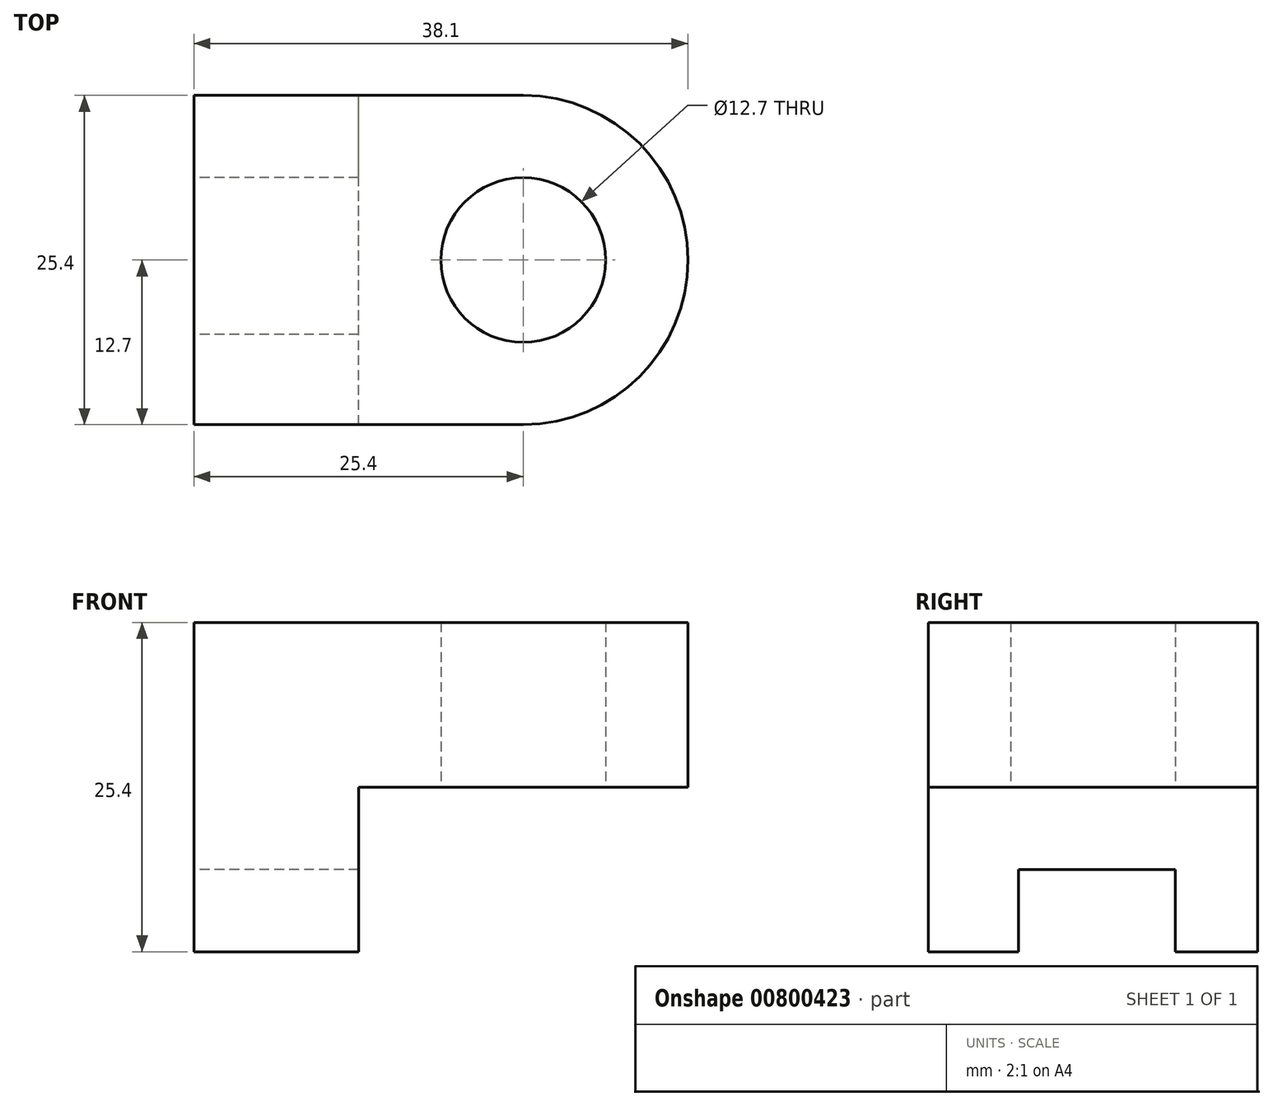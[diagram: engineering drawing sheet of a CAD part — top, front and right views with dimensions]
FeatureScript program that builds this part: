
annotation { "Feature Type Name" : "Feature", "Feature Type Description" : "" }
export const myFeature = defineFeature(function(context is Context, id is Id, definition is map)
    precondition{}
    {
        {
            var Q0;
            Q0=qCreatedBy(makeId("Front.planeOp"),FACE);
            var sketch = newSketch(context, id + "F0", { "sketchPlane" : qUnion([Q0])});
            skLineSegment(sketch, "E0", {"start": v(0, 0) * mm, "end": v(0, -25.4) * mm});
            skLineSegment(sketch, "E1", {"start": v(0, -25.4) * mm, "end": v(12.7, -25.4) * mm});
            skLineSegment(sketch, "E2", {"start": v(12.7, -25.4) * mm, "end": v(12.7, 0) * mm});
            skLineSegment(sketch, "E3", {"start": v(12.7, 0) * mm, "end": v(58.46, 0) * mm});
            skLineSegment(sketch, "E4", {"start": v(58.46, 0) * mm, "end": v(58.46, 12.7) * mm});
            skLineSegment(sketch, "E5", {"start": v(58.46, 12.7) * mm, "end": v(0, 12.7) * mm});
            skLineSegment(sketch, "E6", {"start": v(0, 12.7) * mm, "end": v(0, 0) * mm});
            skSolve(sketch);
        }
        {
            var Q0;
            Q0 = qSketchRegion(id + "F0", true);
            extrude(context, id + "F1", {"entities" : qUnion([Q0]), "depth" : 25.4 * mm, "offsetDistance" : 25.4 * mm});
        }
        {
            var Q0;
            Q0=makeQuery(id+"F1.opExtrude","SWEPT_FACE",FACE,{"disambiguationData":[OSD([sQuery(id+"F0.wireOp",EDGE,"E3")])]});
            var sketch = newSketch(context, id + "F2", { "sketchPlane" : qUnion([Q0])});
            skLineSegment(sketch, "E7", {"start": v(12.7, 25.4) * mm, "end": v(25.4, 25.4) * mm, "construction": true});
            skArc(sketch, "E8", {"start": v(25.4, 0) * mm, "mid": v(38.1, 12.7) * mm, "end": v(25.4, 25.4) * mm});
            skCircle(sketch, "E9", {"center": v(25.4, 12.7) * mm, "radius": 6.35 * mm});
            skSolve(sketch);
        }
        {
            var Q0;
            Q0 = qSketchRegion(id + "F2", true);
            var Q1;
            {var subQ0=sQuery(id+"F2.wireOp",EDGE,"E8");Q1=makeQuery(id+"F2.imprint","IMPRINT",FACE,{"disambiguationData":[TD([[makeQuery(id+"F2.imprint","IMPRINT",EDGE,{"derivedFrom":subQ0}),-1.0]])]});}
            extrude(context, id + "F3", {"entities" : qUnion([Q0, Q1]), "operationType" : NewBodyOperationType.REMOVE, "endBound" : BoundingType.UP_TO_NEXT, "oppositeDirection" : true, "depth" : 25.4 * mm, "offsetDistance" : 25.4 * mm});
        }
        {
            var Q0;
            Q0 = qSketchRegion(id + "FvnkUKrbXFRG5vN_1", true);
            var Q1;
            Q1=makeQuery(id+"F1.opExtrude","SWEPT_FACE",FACE,{"disambiguationData":[OSD([sQuery(id+"F0.wireOp",EDGE,"E2")])]});
            extrude(context, id + "F4", {"entities" : qUnion([Q0, Q1]), "operationType" : NewBodyOperationType.REMOVE, "oppositeDirection" : true, "depth" : 25.4 * mm, "offsetDistance" : 25.4 * mm});
        }
        {
            var Q0;
            {var subQ0=sQuery(id+"F0.wireOp",EDGE,"E3");Q0=makeQuery(id+"F4.boolean.opBoolean","MERGE",FACE,{"derivedFrom":[makeQuery(id+"F1.opExtrude","SWEPT_FACE",FACE,{"disambiguationData":[OSD([subQ0])]}),makeQuery(id+"F4.opExtrude","SWEPT_FACE",FACE,{"disambiguationData":[OSD([sQuery(id+"F0.wireOp",EDGE,"E2"),subQ0])]})]});}
            var sketch = newSketch(context, id + "F5", { "sketchPlane" : qUnion([Q0])});
            skLineSegment(sketch, "E10", {"start": v(0, 25.4) * mm, "end": v(12.7, 25.4) * mm, "construction": true});
            skLineSegment(sketch, "E11", {"start": v(12.7, 25.4) * mm, "end": v(12.7, 0) * mm});
            skSolve(sketch);
        }
        {
            var Q0;
            {var subQ0=sQuery(id+"F5.wireOp",EDGE,"E11");Q0=makeQuery(id+"F5.imprint","IMPRINT",FACE,{"disambiguationData":[TD([[makeQuery(id+"F5.imprint","IMPRINT",EDGE,{"derivedFrom":subQ0}),-1.0]])]});}
            extrude(context, id + "F6", {"entities" : qUnion([Q0]), "operationType" : NewBodyOperationType.ADD, "depth" : 12.7 * mm, "offsetDistance" : 25.4 * mm});
        }
        {
            var Q0;
            Q0=makeQuery(id+"F6.opExtrude","CAP_FACE",FACE,{"disambiguationData":[OSD([sQuery(id+"F0.wireOp",EDGE,"E0"),sQuery(id+"F0.wireOp",EDGE,"E2"),sQuery(id+"F0.wireOp",EDGE,"E3"),sQuery(id+"F0.wireOp",EDGE,"E6"),sQuery(id+"F5.wireOp",EDGE,"E11")])],"isStart":false});
            var sketch = newSketch(context, id + "F7", { "sketchPlane" : qUnion([Q0])});
            skLineSegment(sketch, "E12", {"start": v(12.7, 25.4) * mm, "end": v(12.7, 19.05) * mm, "construction": true});
            skLineSegment(sketch, "E13", {"start": v(12.7, 19.05) * mm, "end": v(12.7, 25.4) * mm, "construction": true});
            skLineSegment(sketch, "E14", {"start": v(12.7, 25.4) * mm, "end": v(12.7, 12.7) * mm, "construction": true});
            skLineSegment(sketch, "E15", {"start": v(12.7, 12.7) * mm, "end": v(12.7, 6.35) * mm, "construction": true});
            skLineSegment(sketch, "E16", {"start": v(12.7, 18.45) * mm, "end": v(0, 18.45) * mm});
            skLineSegment(sketch, "E17", {"start": v(12.7, 6.35) * mm, "end": v(0, 6.35) * mm});
            skSolve(sketch);
        }
        {
            var Q0;
            Q0 = qSketchRegion(id + "F7", true);
            var Q1;
            {var subQ0=sQuery(id+"F7.wireOp",EDGE,"E16");Q1=makeQuery(id+"F7.imprint","IMPRINT",FACE,{"disambiguationData":[TD([[makeQuery(id+"F7.imprint","IMPRINT",EDGE,{"derivedFrom":subQ0}),1.0]])]});}
            extrude(context, id + "F8", {"entities" : qUnion([Q0, Q1]), "operationType" : NewBodyOperationType.REMOVE, "oppositeDirection" : true, "depth" : 6.35 * mm, "offsetDistance" : 25.4 * mm});
        }
    });
